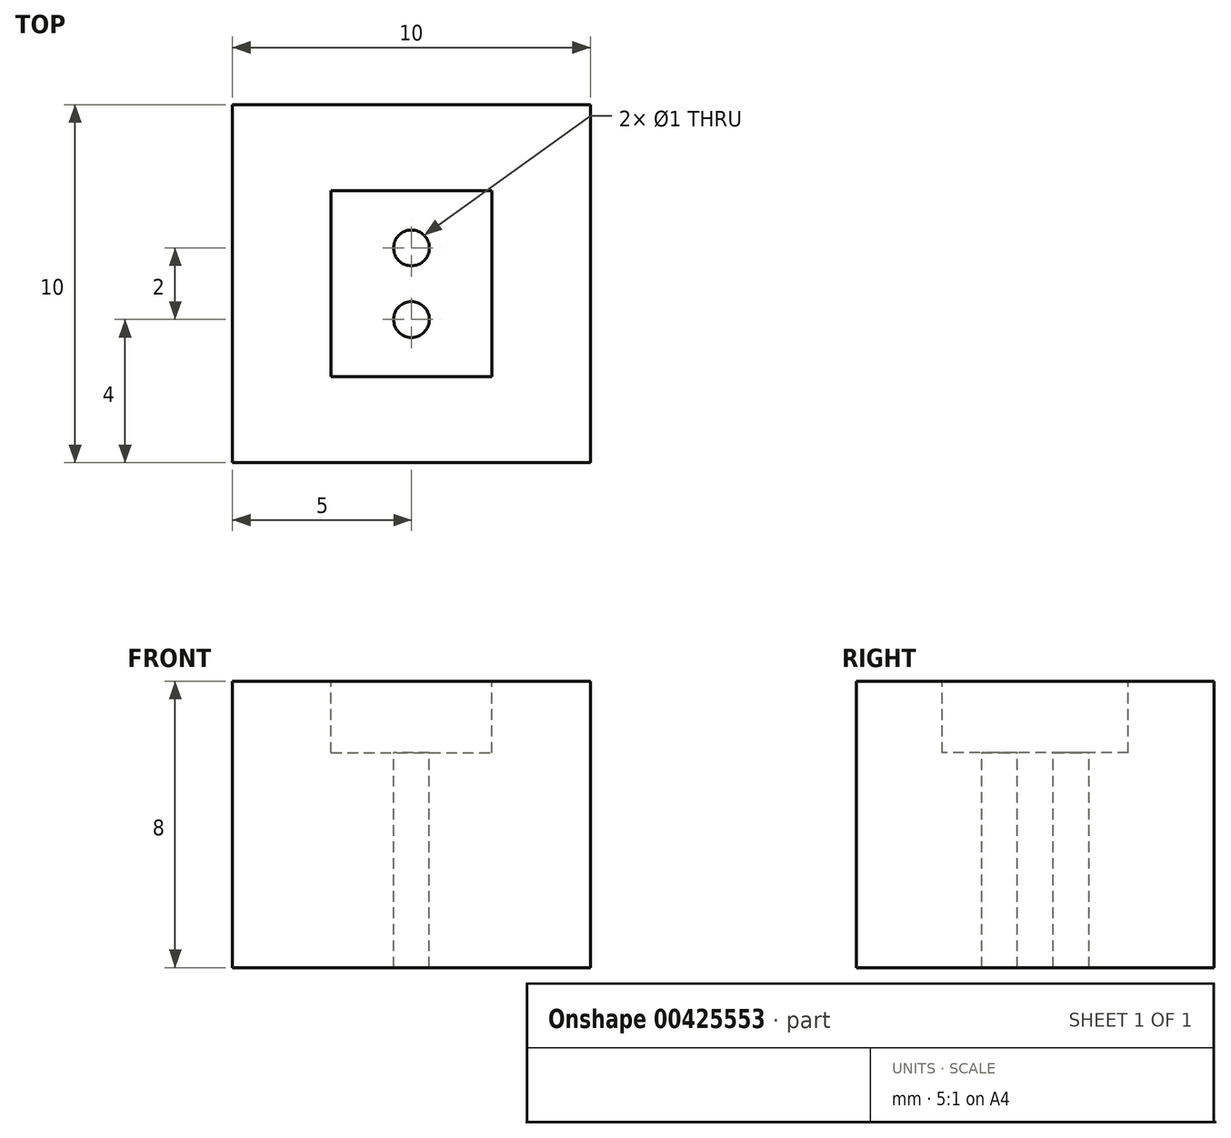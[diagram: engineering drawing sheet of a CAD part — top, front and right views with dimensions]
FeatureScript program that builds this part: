
annotation { "Feature Type Name" : "Feature", "Feature Type Description" : "" }
export const myFeature = defineFeature(function(context is Context, id is Id, definition is map)
    precondition{}
    {
        {
            var Q0;
            Q0=qCreatedBy(makeId("Top.planeOp"),FACE);
            var sketch = newSketch(context, id + "F0", { "sketchPlane" : qUnion([Q0])});
            skLineSegment(sketch, "E0.bottom", {"start": v(0, 0) * mm, "end": v(10, 0) * mm});
            skLineSegment(sketch, "E0.top", {"start": v(0, -10) * mm, "end": v(10, -10) * mm});
            skLineSegment(sketch, "E0.left", {"start": v(0, 0) * mm, "end": v(0, -10) * mm});
            skLineSegment(sketch, "E0.right", {"start": v(10, 0) * mm, "end": v(10, -10) * mm});
            skSolve(sketch);
        }
        {
            var Q0;
            Q0=makeQuery(id+"F0.imprint","IMPRINT",FACE,{"disambiguationData":[TD([[makeQuery(id+"F0.imprint","IMPRINT",EDGE,{"derivedFrom":sQuery(id+"F0.wireOp",EDGE,"E0.bottom")}),-1.0]])]});
            extrude(context, id + "F1", {"entities" : qUnion([Q0]), "depth" : 8 * mm});
        }
        {
            var Q0;
            Q0=makeQuery(id+"F1.opExtrude","CAP_FACE",FACE,{"disambiguationData":[OSD([sQuery(id+"F0.wireOp",EDGE,"E0.bottom"),sQuery(id+"F0.wireOp",EDGE,"E0.top"),sQuery(id+"F0.wireOp",EDGE,"E0.left"),sQuery(id+"F0.wireOp",EDGE,"E0.right")])],"isStart":false});
            var sketch = newSketch(context, id + "F2", { "sketchPlane" : qUnion([Q0])});
            skLineSegment(sketch, "E1.bottom", {"start": v(2.75, -2.4) * mm, "end": v(7.25, -2.4) * mm});
            skLineSegment(sketch, "E1.top", {"start": v(2.75, -7.6) * mm, "end": v(7.25, -7.6) * mm});
            skLineSegment(sketch, "E1.left", {"start": v(2.75, -2.4) * mm, "end": v(2.75, -7.6) * mm});
            skLineSegment(sketch, "E1.right", {"start": v(7.25, -2.4) * mm, "end": v(7.25, -7.6) * mm});
            skSolve(sketch);
        }
        {
            var Q0;
            Q0=makeQuery(id+"F2.imprint","IMPRINT",FACE,{"disambiguationData":[TD([[makeQuery(id+"F2.imprint","IMPRINT",EDGE,{"derivedFrom":sQuery(id+"F2.wireOp",EDGE,"E1.bottom")}),-1.0]])]});
            extrude(context, id + "F3", {"entities" : qUnion([Q0]), "operationType" : NewBodyOperationType.REMOVE, "oppositeDirection" : true, "depth" : 2 * mm});
        }
        {
            var Q0;
            Q0=makeQuery(id+"F3.boolean.opBoolean","COPY",FACE,{"derivedFrom":makeQuery(id+"F3.opExtrude","CAP_FACE",FACE,{"disambiguationData":[OSD([sQuery(id+"F2.wireOp",EDGE,"E1.bottom"),sQuery(id+"F2.wireOp",EDGE,"E1.top"),sQuery(id+"F2.wireOp",EDGE,"E1.left"),sQuery(id+"F2.wireOp",EDGE,"E1.right")])],"isStart":false})});
            var sketch = newSketch(context, id + "F4", { "sketchPlane" : qUnion([Q0])});
            skCircle(sketch, "E2", {"center": v(5, -4) * mm, "radius": 0.5 * mm});
            skCircle(sketch, "E3", {"center": v(5, -6) * mm, "radius": 0.5 * mm});
            skSolve(sketch);
        }
        {
            var Q0;
            Q0=makeQuery(id+"F4.imprint","IMPRINT",FACE,{"disambiguationData":[TD([[makeQuery(id+"F4.imprint","IMPRINT",EDGE,{"derivedFrom":sQuery(id+"F4.wireOp",EDGE,"E2")}),1.0]])]});
            var Q1;
            Q1=makeQuery(id+"F4.imprint","IMPRINT",FACE,{"disambiguationData":[TD([[makeQuery(id+"F4.imprint","IMPRINT",EDGE,{"derivedFrom":sQuery(id+"F4.wireOp",EDGE,"E3")}),1.0]])]});
            extrude(context, id + "F5", {"entities" : qUnion([Q0, Q1]), "operationType" : NewBodyOperationType.REMOVE, "oppositeDirection" : true, "depth" : 25 * mm});
        }
    });
